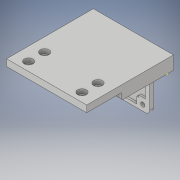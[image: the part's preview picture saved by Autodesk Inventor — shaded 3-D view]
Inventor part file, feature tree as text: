
AUTODESK INVENTOR PART (.ipt)
format: ipt  version: 2019 (Build 230136000, 136)  size: 201,728 bytes
history: native  units: mm
features: sketch x7, extrude x4, fillet x3, hole x2
ambient origin geometry x8: Origin, YZ Plane, XZ Plane, XY Plane, X Axis, Y Axis, Z Axis, Center Point
bodies: Solid1 (feature_tree)
feature tree (16):
  extrude  "Extrusion1"  Depth=65.0mm
  hole  "Hole1"  [1 undecoded]
  extrude  "Extrusion2"  Depth=40.0mm
  extrude  "Extrusion3"  Depth=60.0mm
  hole  "Hole2"  [1 undecoded]
  sketch  "Sketch6"  dims[d16=26.0mm d17=5.0mm d18=0.0mm]
  extrude  "Extrusion4"  Depth=1.0mm
  fillet  "Fillet1"  Radius=1.8mm
  fillet  "Fillet2"  Radius=17.0mm
  fillet  "Fillet3"  Radius=3.0mm
  sketch  "Sketch1"  dims[d0=60.0mm d1=65.0mm]
  sketch  "Sketch2"  dims[d2=10.0mm d3=0.0mm d4=60.0mm]
  sketch  "Sketch3"  dims[d5=25.0mm d6=40.0mm]
  sketch  "Sketch4"  dims[d7=12.0mm]
  sketch  "Sketch5"  dims[d8=3.2mm d9=6.0mm d10=6.5mm d11=3.25mm d12=90.0deg d13=8.0mm d14=90.0deg d15=60.0mm]
  sketch  "Sketch7"  dims[d19=57.0mm d20=1.25mm d21=1.8mm d22=17.0mm d23=3.0mm d24=34.0mm d25=33.0mm d26=0.0mm d27=16.675mm d28=24.0mm d29=24.0mm d30=3.2mm d31=6.0mm d32=6.5mm d33=3.25mm d34=90.0deg d35=8.0mm d36=90.0deg d37=18.0mm d38=18.0mm d39=28.0mm d40=15.0mm d41=15.0mm d42=28.0mm d43=1.5mm d44=0.0mm d45=5.0mm d46=3.0mm d47=1.0mm]
note: 2 required parameter values undecoded (feature->parameter linkage not recoverable at this tier; creation-order binding heuristic only, values carry confidence <= 0.55)
